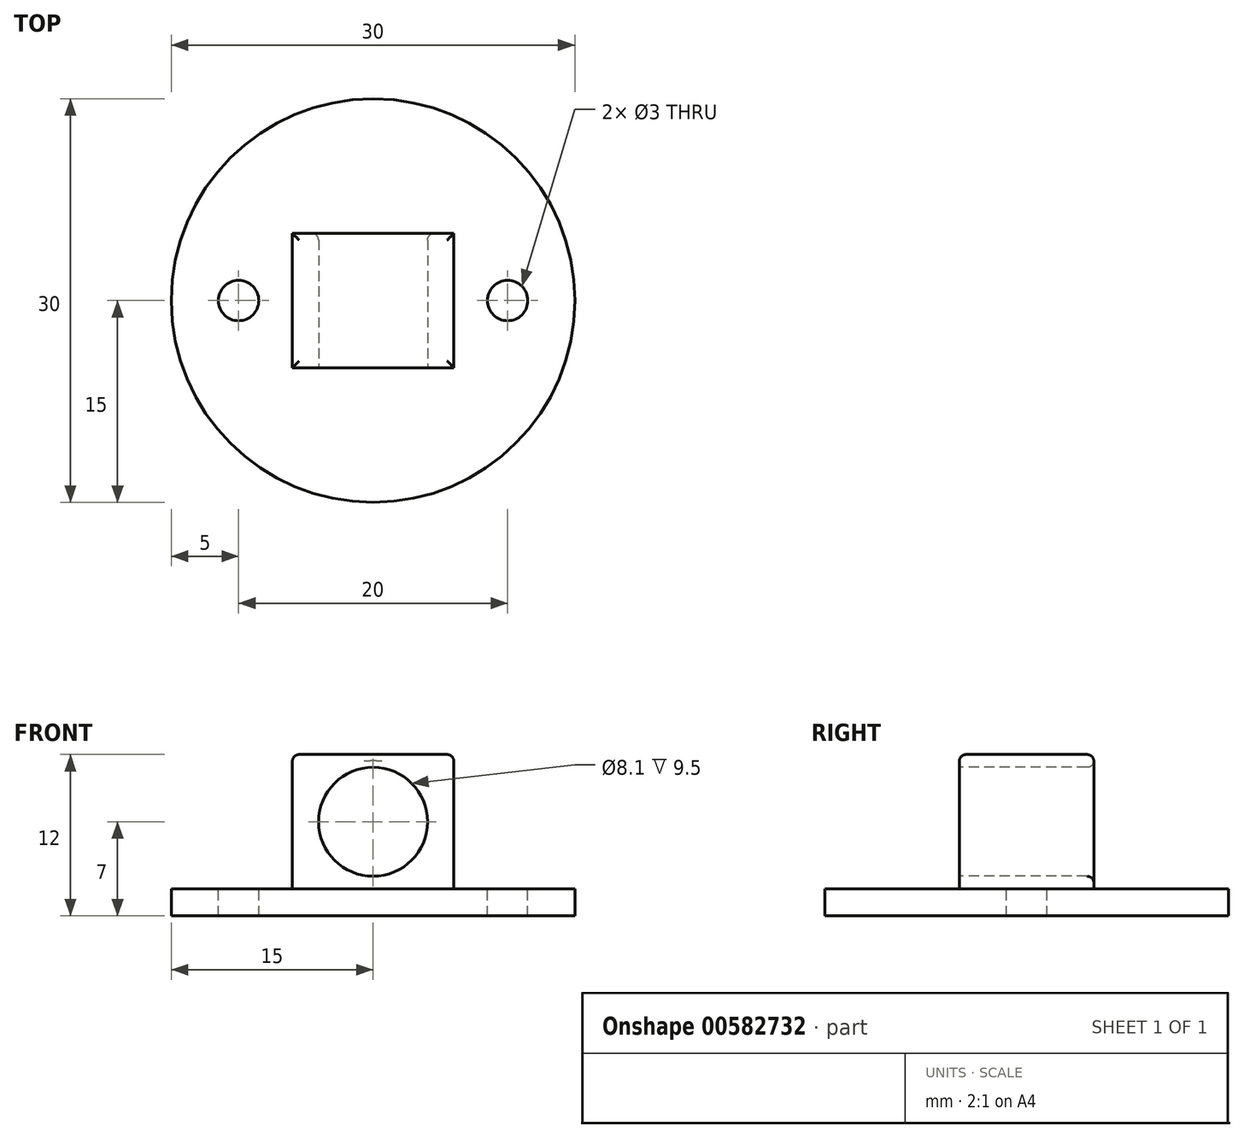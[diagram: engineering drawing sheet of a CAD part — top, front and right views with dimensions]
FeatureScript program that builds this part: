
annotation { "Feature Type Name" : "Feature", "Feature Type Description" : "" }
export const myFeature = defineFeature(function(context is Context, id is Id, definition is map)
    precondition{}
    {
        {
            var Q0;
            Q0=qCreatedBy(makeId("Top.planeOp"),FACE);
            var sketch = newSketch(context, id + "F0", { "sketchPlane" : qUnion([Q0])});
            skCircle(sketch, "E0", {"center": v(0, 0) * mm, "radius": 15 * mm});
            skSolve(sketch);
        }
        {
            var Q0;
            Q0 = qSketchRegion(id + "F0", true);
            extrude(context, id + "F1", {"entities" : qUnion([Q0]), "depth" : 2 * mm, "offsetDistance" : 25 * mm});
        }
        {
            var Q0;
            Q0=makeQuery(id+"F1.opExtrude","CAP_FACE",FACE,{"disambiguationData":[OSD([sQuery(id+"F0.wireOp",EDGE,"E0")])],"isStart":false});
            var sketch = newSketch(context, id + "F2", { "sketchPlane" : qUnion([Q0])});
            skLineSegment(sketch, "E1.bottom", {"start": v(-6, 5) * mm, "end": v(6, 5) * mm});
            skLineSegment(sketch, "E1.top", {"start": v(-6, -5) * mm, "end": v(6, -5) * mm});
            skLineSegment(sketch, "E1.left", {"start": v(-6, 5) * mm, "end": v(-6, -5) * mm});
            skLineSegment(sketch, "E1.right", {"start": v(6, 5) * mm, "end": v(6, -5) * mm});
            skPoint(sketch, "E1.middle", {"position": v(0, 0) * mm});
            skSolve(sketch);
        }
        {
            var Q0;
            Q0 = qSketchRegion(id + "F2", true);
            extrude(context, id + "F3", {"entities" : qUnion([Q0]), "operationType" : NewBodyOperationType.ADD, "depth" : 10 * mm, "offsetDistance" : 25 * mm});
        }
        {
            var Q0;
            Q0=makeQuery(id+"F3.opExtrude","SWEPT_FACE",FACE,{"disambiguationData":[OSD([sQuery(id+"F2.wireOp",EDGE,"E1.top")])]});
            var sketch = newSketch(context, id + "F4", { "sketchPlane" : qUnion([Q0])});
            skCircle(sketch, "E2", {"center": v(0, 7) * mm, "radius": 4.05 * mm});
            skSolve(sketch);
        }
        {
            var Q0;
            Q0 = qSketchRegion(id + "F4", true);
            extrude(context, id + "F5", {"entities" : qUnion([Q0]), "operationType" : NewBodyOperationType.REMOVE, "endBound" : BoundingType.THROUGH_ALL, "oppositeDirection" : true, "depth" : 25 * mm, "offsetDistance" : 25 * mm});
        }
        {
            var Q0;
            Q0=makeQuery(id+"F1.opExtrude","CAP_FACE",FACE,{"disambiguationData":[OSD([sQuery(id+"F0.wireOp",EDGE,"E0")])],"isStart":false});
            var sketch = newSketch(context, id + "F6", { "sketchPlane" : qUnion([Q0])});
            skCircle(sketch, "E3", {"center": v(10, 0) * mm, "radius": 1.5 * mm});
            skCircle(sketch, "E4.MirrorC", {"center": v(-10, 0) * mm, "radius": 1.5 * mm});
            skSolve(sketch);
        }
        {
            var Q0;
            Q0 = qSketchRegion(id + "F6", true);
            extrude(context, id + "F7", {"entities" : qUnion([Q0]), "operationType" : NewBodyOperationType.REMOVE, "endBound" : BoundingType.THROUGH_ALL, "oppositeDirection" : true, "depth" : 25 * mm, "offsetDistance" : 25 * mm});
        }
        {
            var Q0;
            Q0=makeQuery(id+"F5.boolean.opBoolean","INTERSECT",EDGE,{"derivedFrom":[makeQuery(id+"F3.opExtrude","SWEPT_FACE",FACE,{"disambiguationData":[OSD([sQuery(id+"F2.wireOp",EDGE,"E1.bottom")])]}),makeQuery(id+"F5.opExtrude","SWEPT_FACE",FACE,{"disambiguationData":[OSD([sQuery(id+"F4.wireOp",EDGE,"E2")])]})]});
            var Q1;
            Q1=makeQuery(id+"F5.boolean.opBoolean","COPY",EDGE,{"derivedFrom":makeQuery(id+"F5.opExtrude","CAP_EDGE",EDGE,{"disambiguationData":[OSD([sQuery(id+"F4.wireOp",EDGE,"E2")])],"isStart":true})});
            var Q2;
            Q2=makeQuery(id+"F3.opExtrude","CAP_EDGE",EDGE,{"disambiguationData":[OSD([sQuery(id+"F2.wireOp",EDGE,"E1.top")])],"isStart":false});
            var Q3;
            Q3=makeQuery(id+"F3.opExtrude","CAP_EDGE",EDGE,{"disambiguationData":[OSD([sQuery(id+"F2.wireOp",EDGE,"E1.right")])],"isStart":false});
            var Q4;
            Q4=makeQuery(id+"F3.opExtrude","CAP_EDGE",EDGE,{"disambiguationData":[OSD([sQuery(id+"F2.wireOp",EDGE,"E1.bottom")])],"isStart":false});
            var Q5;
            Q5=makeQuery(id+"F3.opExtrude","CAP_EDGE",EDGE,{"disambiguationData":[OSD([sQuery(id+"F2.wireOp",EDGE,"E1.left")])],"isStart":false});
            var Q6;
            Q6=makeQuery(id+"F3.opExtrude","CAP_EDGE",EDGE,{"disambiguationData":[OSD([sQuery(id+"F2.wireOp",EDGE,"E1.left")])],"isStart":true});
            var Q7;
            Q7=makeQuery(id+"F3.opExtrude","CAP_EDGE",EDGE,{"disambiguationData":[OSD([sQuery(id+"F2.wireOp",EDGE,"E1.right")])],"isStart":true});
            fillet(context, id + "F8", {"entities" : qUnion([Q0, Q1, Q2, Q3, Q4, Q5, Q6, Q7]), "radius" : 0.5 * mm, "tangentPropagation" : true, "allowEdgeOverflow" : false});
        }
    });
